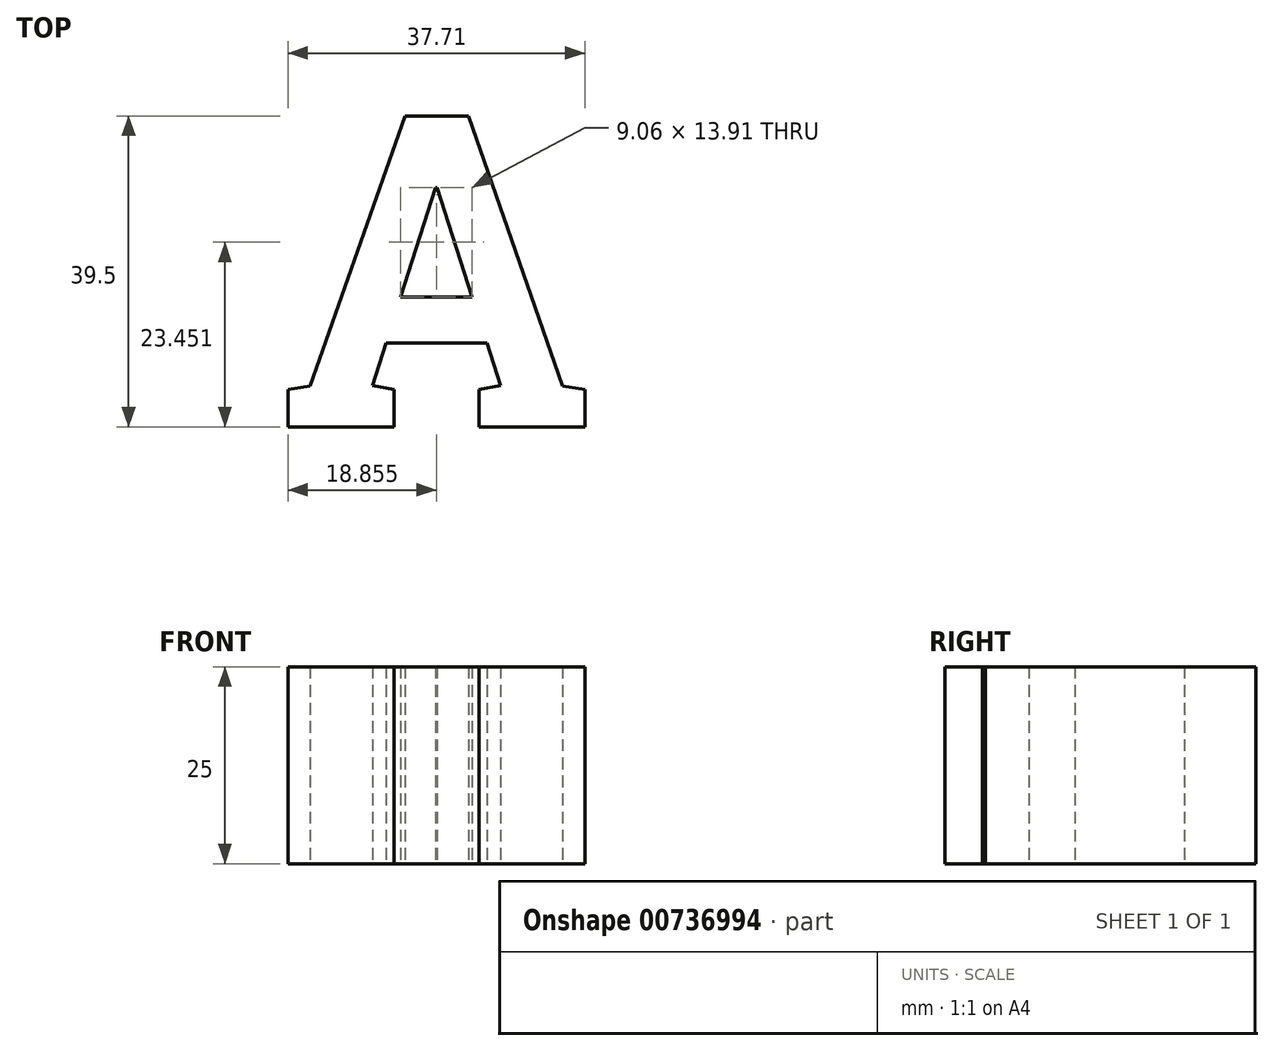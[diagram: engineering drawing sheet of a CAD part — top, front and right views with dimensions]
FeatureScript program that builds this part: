
annotation { "Feature Type Name" : "Feature", "Feature Type Description" : "" }
export const myFeature = defineFeature(function(context is Context, id is Id, definition is map)
    precondition{}
    {
        {
            var Q0;
            Q0=qCreatedBy(makeId("Top.planeOp"),FACE);
            var sketch = newSketch(context, id + "F0", { "sketchPlane" : qUnion([Q0])});
            skText(sketch, "E0", { "text": "A", "fontName": "RobotoSlab-Bold.ttf"});
            const initialGuessF0  = {"E0": [0, -0.04, 1, 0, 0.04]};
            skSetInitialGuess(sketch, initialGuessF0);
            skSolve(sketch);
        }
        {
            var Q0;
            Q0=makeQuery(id+"FFE8gVDdY02I8df_0.opExtrude","CAP_FACE",FACE,{"disambiguationData":[OSD([sQuery(id+"F0.wireOp",EDGE,"E0.sketch_text.stroke-0"),sQuery(id+"F0.wireOp",EDGE,"E0.sketch_text.stroke-1"),sQuery(id+"F0.wireOp",EDGE,"E0.sketch_text.stroke-2"),sQuery(id+"F0.wireOp",EDGE,"E0.sketch_text.stroke-3"),sQuery(id+"F0.wireOp",EDGE,"E0.sketch_text.stroke-4"),sQuery(id+"F0.wireOp",EDGE,"E0.sketch_text.stroke-5"),sQuery(id+"F0.wireOp",EDGE,"E0.sketch_text.stroke-6"),sQuery(id+"F0.wireOp",EDGE,"E0.sketch_text.stroke-7"),sQuery(id+"F0.wireOp",EDGE,"E0.sketch_text.stroke-8"),sQuery(id+"F0.wireOp",EDGE,"E0.sketch_text.stroke-9"),sQuery(id+"F0.wireOp",EDGE,"E0.sketch_text.stroke-10"),sQuery(id+"F0.wireOp",EDGE,"E0.sketch_text.stroke-11"),sQuery(id+"F0.wireOp",EDGE,"E0.sketch_text.stroke-12"),sQuery(id+"F0.wireOp",EDGE,"E0.sketch_text.stroke-13"),sQuery(id+"F0.wireOp",EDGE,"E0.sketch_text.stroke-14"),sQuery(id+"F0.wireOp",EDGE,"E0.sketch_text.stroke-15"),sQuery(id+"F0.wireOp",EDGE,"E0.sketch_text.stroke-16"),sQuery(id+"F0.wireOp",EDGE,"E0.sketch_text.stroke-17"),sQuery(id+"F0.wireOp",EDGE,"E0.sketch_text.stroke-18"),sQuery(id+"F0.wireOp",EDGE,"E0.sketch_text.stroke-19")])],"isStart":false});
            var sketch = newSketch(context, id + "F1", { "sketchPlane" : qUnion([Q0])});
            skLineSegment(sketch, "E1.0", {"start": v(3.63, -34.48) * mm, "end": v(0.71, -34.9) * mm});
            skLineSegment(sketch, "E1.1", {"start": v(15.67, -0.1) * mm, "end": v(3.63, -34.48) * mm});
            skLineSegment(sketch, "E1.2", {"start": v(24.35, -0.1) * mm, "end": v(15.67, -0.1) * mm});
            skLineSegment(sketch, "E1.3", {"start": v(36.3, -34.48) * mm, "end": v(24.35, -0.1) * mm});
            skLineSegment(sketch, "E1.4", {"start": v(39.22, -34.9) * mm, "end": v(36.3, -34.48) * mm});
            skLineSegment(sketch, "E1.5", {"start": v(12.35, -34.45) * mm, "end": v(13.86, -29.74) * mm});
            skLineSegment(sketch, "E1.6", {"start": v(14.97, -34.92) * mm, "end": v(12.35, -34.45) * mm});
            skLineSegment(sketch, "E1.7", {"start": v(14.97, -40.4) * mm, "end": v(14.97, -34.92) * mm});
            skLineSegment(sketch, "E1.8", {"start": v(0.71, -40.4) * mm, "end": v(14.97, -40.4) * mm});
            skLineSegment(sketch, "E1.9", {"start": v(13.86, -29.74) * mm, "end": v(26.08, -29.74) * mm});
            skLineSegment(sketch, "E1.10", {"start": v(26.08, -29.74) * mm, "end": v(27.59, -34.45) * mm});
            skLineSegment(sketch, "E1.11", {"start": v(27.59, -34.45) * mm, "end": v(24.96, -34.92) * mm});
            skLineSegment(sketch, "E1.12", {"start": v(24.96, -34.92) * mm, "end": v(24.96, -40.4) * mm});
            skLineSegment(sketch, "E1.13", {"start": v(24.96, -40.4) * mm, "end": v(39.22, -40.4) * mm});
            skLineSegment(sketch, "E1.14", {"start": v(0.71, -34.9) * mm, "end": v(0.71, -40.4) * mm});
            skLineSegment(sketch, "E1.15", {"start": v(39.22, -40.4) * mm, "end": v(39.22, -34.9) * mm});
            skLineSegment(sketch, "E2.0", {"start": v(19.97, -10.66) * mm, "end": v(15.98, -23.1) * mm});
            skLineSegment(sketch, "E2.1", {"start": v(23.95, -23.1) * mm, "end": v(19.97, -10.66) * mm});
            skLineSegment(sketch, "E2.2", {"start": v(15.98, -23.1) * mm, "end": v(23.95, -23.1) * mm});
            skLineSegment(sketch, "E3.0", {"start": v(3.04, -33.76) * mm, "end": v(-0.09, -34.21) * mm});
            skLineSegment(sketch, "E3.1", {"start": v(15.1, 0.7) * mm, "end": v(3.04, -33.76) * mm});
            skLineSegment(sketch, "E3.2", {"start": v(24.92, 0.7) * mm, "end": v(15.1, 0.7) * mm});
            skLineSegment(sketch, "E3.3", {"start": v(36.9, -33.76) * mm, "end": v(24.92, 0.7) * mm});
            skLineSegment(sketch, "E3.4", {"start": v(40.02, -34.21) * mm, "end": v(36.9, -33.76) * mm});
            skLineSegment(sketch, "E3.5", {"start": v(13.4, -33.82) * mm, "end": v(14.44, -30.54) * mm});
            skLineSegment(sketch, "E3.6", {"start": v(15.77, -34.25) * mm, "end": v(13.4, -33.82) * mm});
            skLineSegment(sketch, "E3.7", {"start": v(15.77, -41.2) * mm, "end": v(15.77, -34.25) * mm});
            skLineSegment(sketch, "E3.8", {"start": v(-0.09, -41.2) * mm, "end": v(15.77, -41.2) * mm});
            skLineSegment(sketch, "E3.9", {"start": v(14.44, -30.54) * mm, "end": v(25.5, -30.54) * mm});
            skLineSegment(sketch, "E3.10", {"start": v(25.5, -30.54) * mm, "end": v(26.55, -33.82) * mm});
            skLineSegment(sketch, "E3.11", {"start": v(26.55, -33.82) * mm, "end": v(24.16, -34.25) * mm});
            skLineSegment(sketch, "E3.12", {"start": v(24.16, -34.25) * mm, "end": v(24.16, -41.2) * mm});
            skLineSegment(sketch, "E3.13", {"start": v(24.16, -41.2) * mm, "end": v(40.02, -41.2) * mm});
            skLineSegment(sketch, "E3.14", {"start": v(-0.09, -34.21) * mm, "end": v(-0.09, -41.2) * mm});
            skLineSegment(sketch, "E3.15", {"start": v(40.02, -41.2) * mm, "end": v(40.02, -34.21) * mm});
            skLineSegment(sketch, "E4.0", {"start": v(19.97, -13.28) * mm, "end": v(17.08, -22.3) * mm});
            skLineSegment(sketch, "E4.1", {"start": v(22.85, -22.3) * mm, "end": v(19.97, -13.28) * mm});
            skLineSegment(sketch, "E4.2", {"start": v(17.08, -22.3) * mm, "end": v(22.85, -22.3) * mm});
            skSolve(sketch);
        }
        {
            var Q0;
            Q0 = qSketchRegion(id + "F0", true);
            extrude(context, id + "F2", {"entities" : qUnion([Q0]), "depth" : 25 * mm, "offsetDistance" : 25 * mm});
        }
    });
